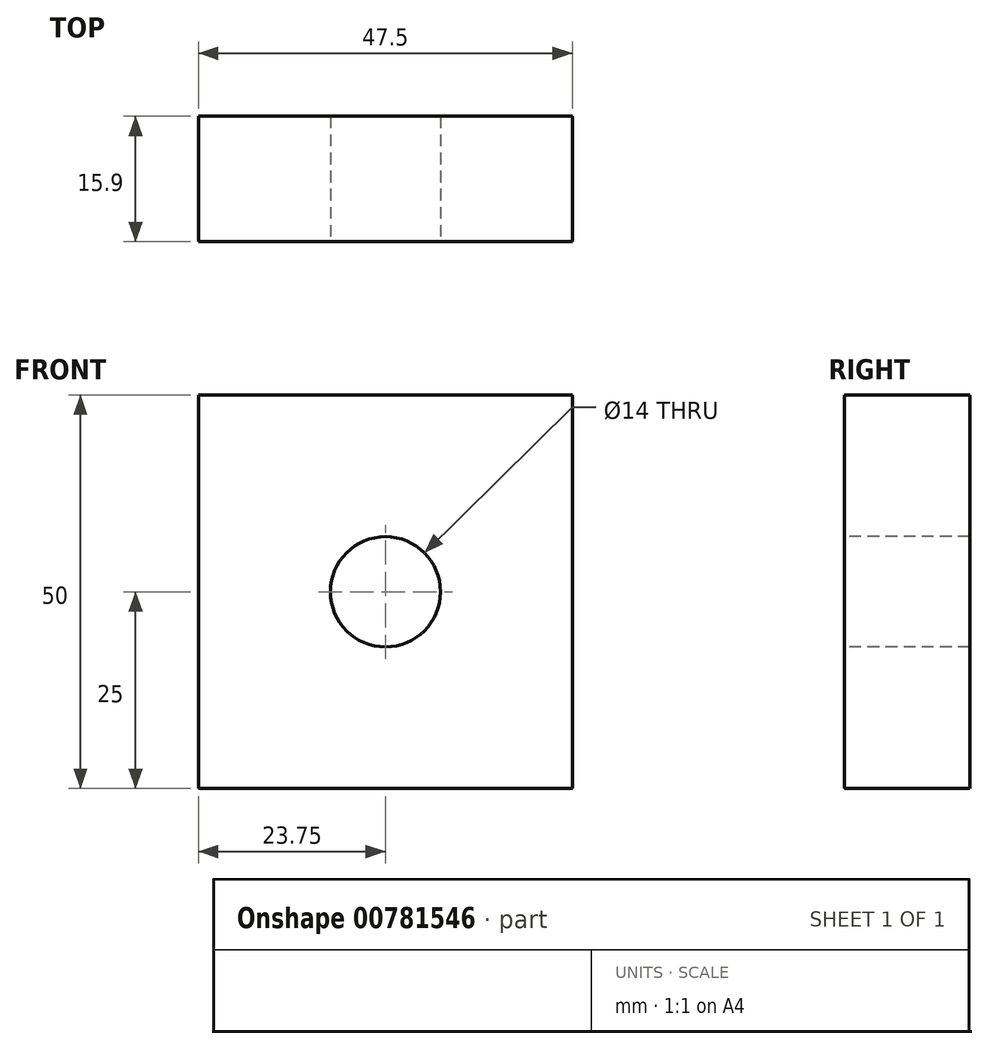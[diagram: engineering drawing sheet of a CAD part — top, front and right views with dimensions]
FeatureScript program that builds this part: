
annotation { "Feature Type Name" : "Feature", "Feature Type Description" : "" }
export const myFeature = defineFeature(function(context is Context, id is Id, definition is map)
    precondition{}
    {
        {
            var Q0;
            Q0=qCreatedBy(makeId("Top.planeOp"),FACE);
            var sketch = newSketch(context, id + "F0", { "sketchPlane" : qUnion([Q0])});
            skLineSegment(sketch, "E0.bottom", {"start": v(0, 0) * mm, "end": v(47.5, 0) * mm});
            skLineSegment(sketch, "E0.top", {"start": v(0, -15.9) * mm, "end": v(47.5, -15.9) * mm});
            skLineSegment(sketch, "E0.left", {"start": v(0, 0) * mm, "end": v(0, -15.9) * mm});
            skLineSegment(sketch, "E0.right", {"start": v(47.5, 0) * mm, "end": v(47.5, -15.9) * mm});
            skSolve(sketch);
        }
        {
            var Q0;
            Q0=makeQuery(id+"F0.imprint","IMPRINT",FACE,{"disambiguationData":[TD([[makeQuery(id+"F0.imprint","IMPRINT",EDGE,{"derivedFrom":sQuery(id+"F0.wireOp",EDGE,"E0.bottom")}),-1.0]])]});
            extrude(context, id + "F1", {"entities" : qUnion([Q0]), "depth" : 50 * mm, "offsetDistance" : 25 * mm});
        }
        {
            var Q0;
            Q0=makeQuery(id+"F1.opExtrude","SWEPT_FACE",FACE,{"disambiguationData":[OSD([sQuery(id+"F0.wireOp",EDGE,"E0.top")])]});
            var sketch = newSketch(context, id + "F2", { "sketchPlane" : qUnion([Q0])});
            skLineSegment(sketch, "E1", {"start": v(47.5, 25) * mm, "end": v(0, 25) * mm});
            skLineSegment(sketch, "E2", {"start": v(23.75, 50) * mm, "end": v(23.75, 0) * mm});
            skPoint(sketch, "E3", {"position": v(23.75, 25) * mm});
            skSolve(sketch);
        }
        {
            var Q0;
            Q0=sQuery(id+"F2.wireOp",VERTEX,"E3");
            var Q1;
            Q1=makeQuery(id+"F1.opExtrude","SWEPT_BODY",BODY,{"disambiguationData":[OSD([sQuery(id+"F0.wireOp",EDGE,"E0.bottom"),sQuery(id+"F0.wireOp",EDGE,"E0.top"),sQuery(id+"F0.wireOp",EDGE,"E0.left"),sQuery(id+"F0.wireOp",EDGE,"E0.right")])]});
            hole(context, id + "F3", {"style" : HoleStyle.SIMPLE, "endStyle" : HoleEndStyle.THROUGH, "holeDiameter" : 14 * mm, "majorDiameter" : 5 * mm, "isTappedThrough" : true, "tappedDepth" : 12 * mm, "tapClearance" : 3, "locations" : qUnion([Q0]), "scope" : qUnion([Q1])});
        }
    });
